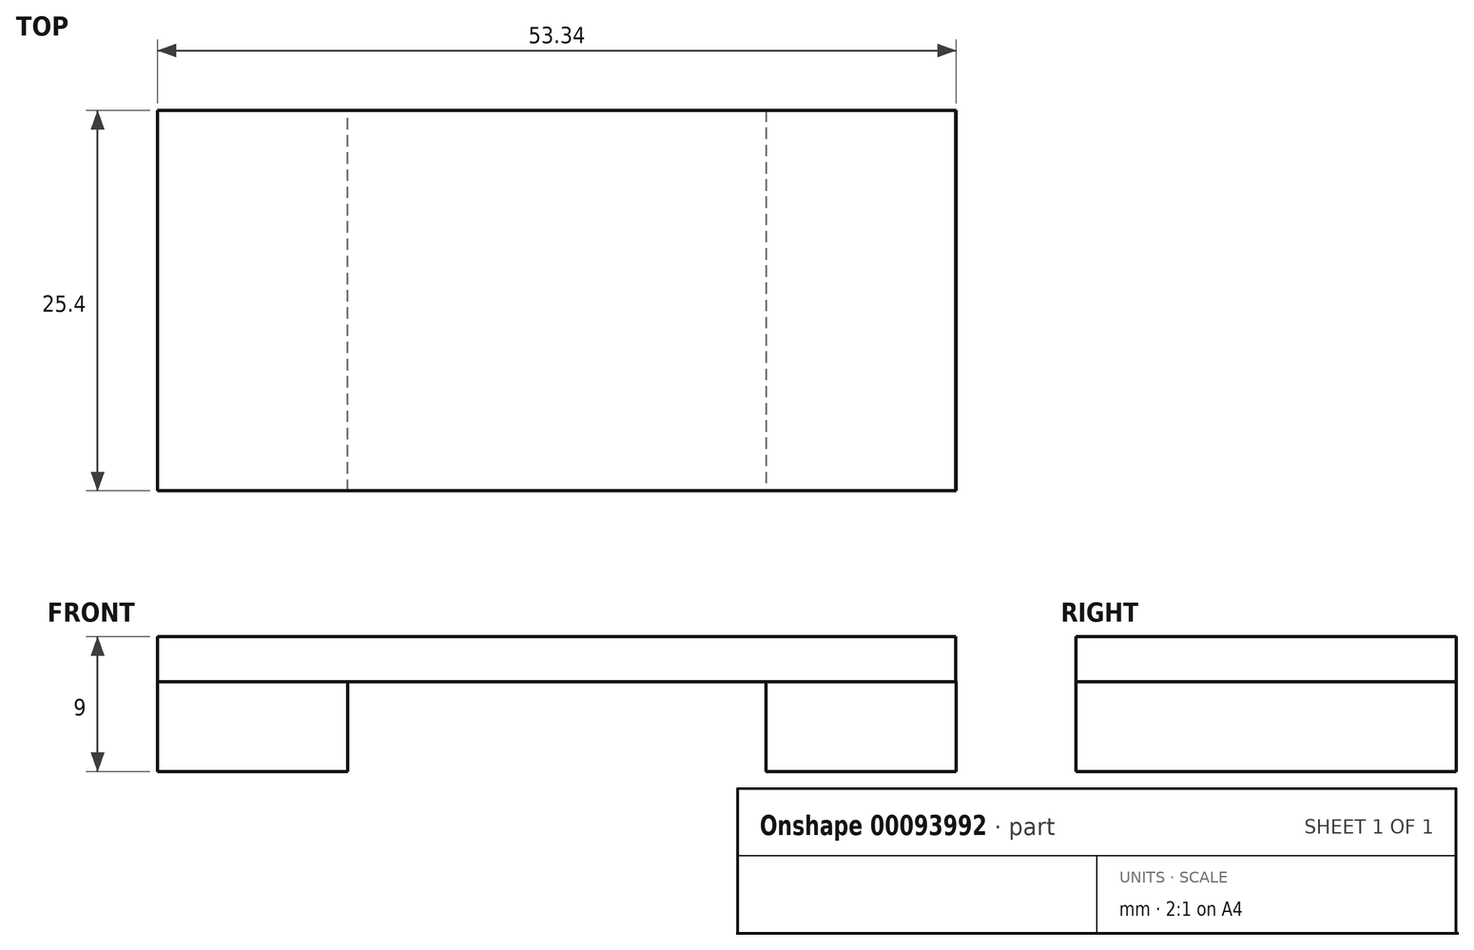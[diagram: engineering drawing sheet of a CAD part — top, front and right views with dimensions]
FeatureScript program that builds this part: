
annotation { "Feature Type Name" : "Feature", "Feature Type Description" : "" }
export const myFeature = defineFeature(function(context is Context, id is Id, definition is map)
    precondition{}
    {
        {
            var Q0;
            Q0=qCreatedBy(makeId("Top.planeOp"),FACE);
            var sketch = newSketch(context, id + "F0", { "sketchPlane" : qUnion([Q0])});
            skLineSegment(sketch, "E0.bottom", {"start": v(0, 0) * mm, "end": v(12.7, 0) * mm});
            skLineSegment(sketch, "E0.top", {"start": v(0, 25.4) * mm, "end": v(12.7, 25.4) * mm});
            skLineSegment(sketch, "E0.left", {"start": v(0, 0) * mm, "end": v(0, 25.4) * mm});
            skLineSegment(sketch, "E0.right", {"start": v(12.7, 0) * mm, "end": v(12.7, 25.4) * mm});
            skLineSegment(sketch, "E1.bottom", {"start": v(40.64, 25.4) * mm, "end": v(53.34, 25.4) * mm});
            skLineSegment(sketch, "E1.top", {"start": v(40.64, 0) * mm, "end": v(53.34, 0) * mm});
            skLineSegment(sketch, "E1.left", {"start": v(40.64, 25.4) * mm, "end": v(40.64, 0) * mm});
            skLineSegment(sketch, "E1.right", {"start": v(53.34, 25.4) * mm, "end": v(53.34, 0) * mm});
            skSolve(sketch);
        }
        {
            var Q0;
            Q0=makeQuery(id+"F0.imprint","IMPRINT",FACE,{"disambiguationData":[TD([[makeQuery(id+"F0.imprint","IMPRINT",EDGE,{"derivedFrom":sQuery(id+"F0.wireOp",EDGE,"E0.bottom")}),1.0]])]});
            var Q1;
            Q1=makeQuery(id+"F0.imprint","IMPRINT",FACE,{"disambiguationData":[TD([[makeQuery(id+"F0.imprint","IMPRINT",EDGE,{"derivedFrom":sQuery(id+"F0.wireOp",EDGE,"E1.bottom")}),-1.0]])]});
            extrude(context, id + "F1", {"entities" : qUnion([Q0, Q1]), "depth" : 6 * mm});
        }
        {
            var Q0;
            Q0=makeQuery(id+"F1.opExtrude","CAP_FACE",FACE,{"disambiguationData":[OSD([sQuery(id+"F0.wireOp",EDGE,"E0.bottom"),sQuery(id+"F0.wireOp",EDGE,"E0.top"),sQuery(id+"F0.wireOp",EDGE,"E0.left"),sQuery(id+"F0.wireOp",EDGE,"E0.right")])],"isStart":false});
            var sketch = newSketch(context, id + "F2", { "sketchPlane" : qUnion([Q0])});
            skLineSegment(sketch, "E2.bottom", {"start": v(0, 25.4) * mm, "end": v(53.32, 25.4) * mm});
            skLineSegment(sketch, "E2.top", {"start": v(0, 0) * mm, "end": v(53.32, 0) * mm});
            skLineSegment(sketch, "E2.left", {"start": v(0, 25.4) * mm, "end": v(0, 0) * mm});
            skLineSegment(sketch, "E2.right", {"start": v(53.32, 25.4) * mm, "end": v(53.32, 0) * mm});
            skSolve(sketch);
        }
        {
            var Q0;
            {var subQ2=sQuery(id+"F2.wireOp",EDGE,"E2.right");Q0=makeQuery(id+"F2.imprint","IMPRINT",FACE,{"disambiguationData":[TD([[makeQuery(id+"F2.imprint","IMPRINT",EDGE,{"derivedFrom":subQ2}),-1.0]])]});}
            var Q1;
            {var subQ0=sQuery(id+"F2.wireOp",EDGE,"E2.left");Q1=makeQuery(id+"F2.imprint","IMPRINT",FACE,{"disambiguationData":[TD([[makeQuery(id+"F2.imprint","IMPRINT",EDGE,{"derivedFrom":subQ0}),-1.0]])]});}
            extrude(context, id + "F3", {"entities" : qUnion([Q0, Q1]), "depth" : 3 * mm});
        }
    });
